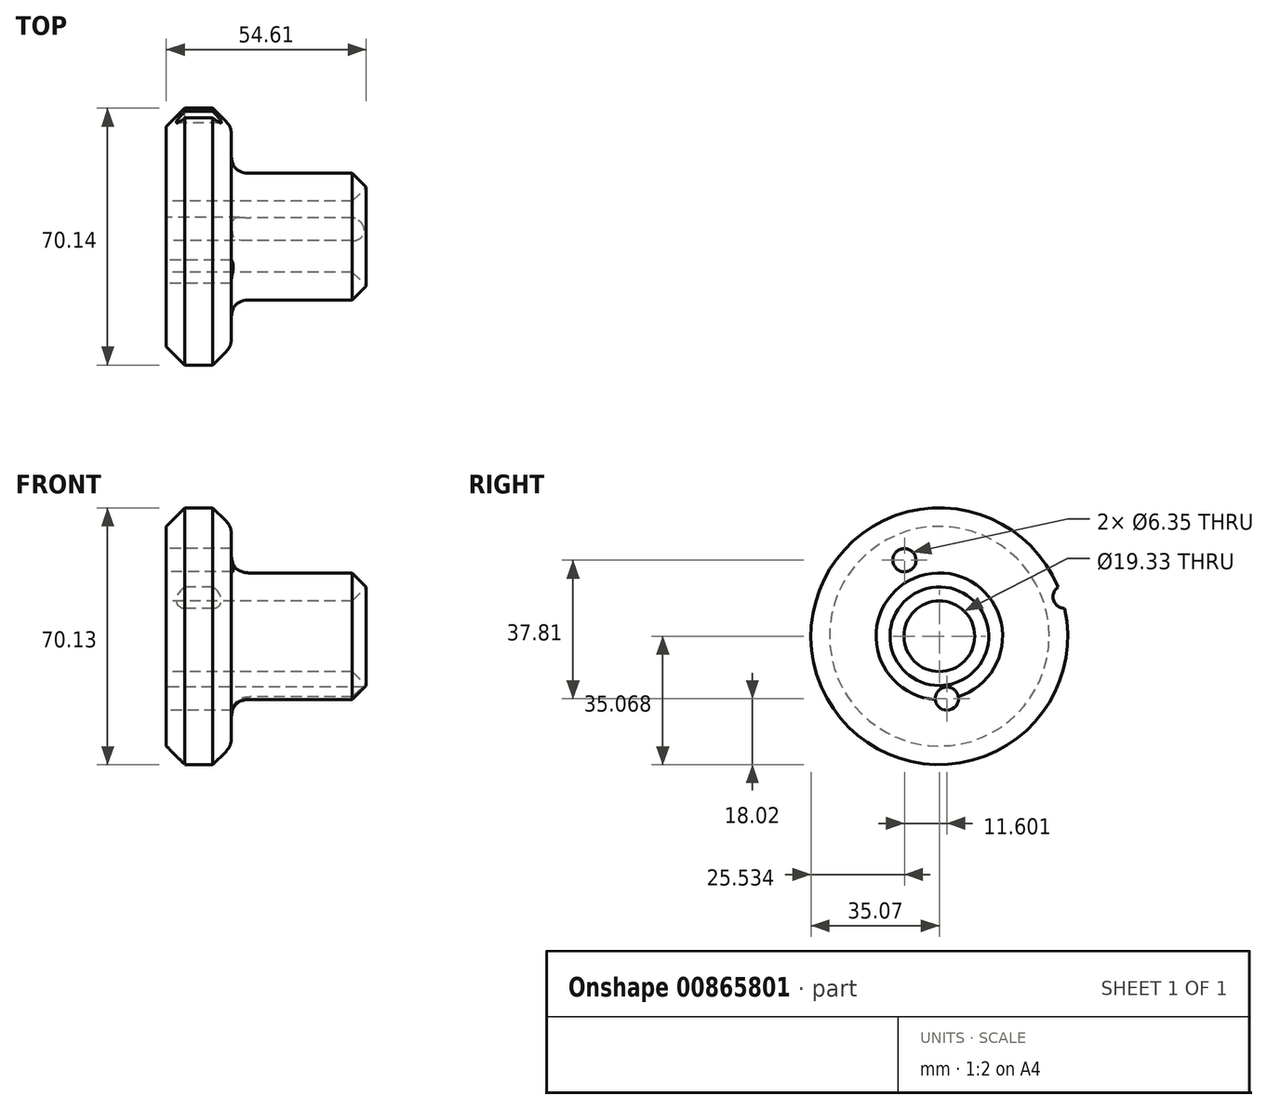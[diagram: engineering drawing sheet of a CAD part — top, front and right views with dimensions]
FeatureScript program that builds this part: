
annotation { "Feature Type Name" : "Feature", "Feature Type Description" : "" }
export const myFeature = defineFeature(function(context is Context, id is Id, definition is map)
    precondition{}
    {
        {
            var Q0;
            Q0=qCreatedBy(makeId("Front.planeOp"),FACE);
            var sketch = newSketch(context, id + "F0", { "sketchPlane" : qUnion([Q0])});
            skLineSegment(sketch, "E0", {"start": v(-39.33, 17.05) * mm, "end": v(50.95, 17.05) * mm, "construction": true});
            skLineSegment(sketch, "E1.bottom", {"start": v(-29.5, 52.11) * mm, "end": v(-11.71, 52.11) * mm});
            skLineSegment(sketch, "E1.top", {"start": v(-29.5, 26.71) * mm, "end": v(-11.71, 26.71) * mm});
            skLineSegment(sketch, "E1.left", {"start": v(-29.5, 52.11) * mm, "end": v(-29.5, 26.71) * mm});
            skLineSegment(sketch, "E1.right", {"start": v(-11.71, 52.11) * mm, "end": v(-11.71, 26.71) * mm});
            skLineSegment(sketch, "E2.bottom", {"start": v(-11.71, 34.33) * mm, "end": v(26.39, 34.33) * mm});
            skLineSegment(sketch, "E2.top", {"start": v(-11.71, 26.71) * mm, "end": v(26.39, 26.71) * mm});
            skLineSegment(sketch, "E2.left", {"start": v(-11.71, 34.33) * mm, "end": v(-11.71, 26.71) * mm});
            skLineSegment(sketch, "E2.right", {"start": v(26.39, 34.33) * mm, "end": v(26.39, 26.71) * mm});
            skSolve(sketch);
        }
        {
            var Q0;
            Q0 = qSketchRegion(id + "F0", true);
            var Q1;
            Q1=sQuery(id+"F0.wireOp",EDGE,"E0");
            revolve(context, id + "F1", {"surfaceOperationType" : NewSurfaceOperationType.NEW, "entities" : qUnion([Q0]), "axis" : qUnion([Q1]), "revolveType" : RevolveType.FULL});
        }
        {
            var Q0;
            Q0=makeQuery(id+"F1.opRevolve","SWEPT_EDGE",EDGE,{"disambiguationData":[OSD([sQuery(id+"F0.wireOp",EDGE,"E1.bottom"),sQuery(id+"F0.wireOp",EDGE,"E1.left")])]});
            var Q1;
            Q1=makeQuery(id+"F1.opRevolve","SWEPT_EDGE",EDGE,{"disambiguationData":[OSD([sQuery(id+"F0.wireOp",EDGE,"E1.bottom"),sQuery(id+"F0.wireOp",EDGE,"E1.right")])]});
            var Q2;
            Q2=makeQuery(id+"F1.opRevolve","SWEPT_EDGE",EDGE,{"disambiguationData":[OSD([sQuery(id+"F0.wireOp",EDGE,"E2.bottom"),sQuery(id+"F0.wireOp",EDGE,"E2.right")])]});
            chamfer(context, id + "F2", {"entities" : qUnion([Q0, Q1, Q2]), "width" : 5.08 * mm, "tangentPropagation" : true});
        }
        {
            var Q0;
            Q0=makeQuery(id+"F1.opRevolve","SWEPT_EDGE",EDGE,{"disambiguationData":[OSD([sQuery(id+"F0.wireOp",EDGE,"E1.right"),sQuery(id+"F0.wireOp",EDGE,"E2.bottom"),sQuery(id+"F0.wireOp",EDGE,"E2.left")])]});
            var Q1;
            {var subQ0=sQuery(id+"F0.wireOp",EDGE,"E1.right");Q1=makeQuery(id+"F2.opChamfer","BLEND_EDGE",EDGE,{"blendedFrom":[makeQuery(id+"F1.opRevolve","SWEPT_EDGE",EDGE,{"disambiguationData":[OSD([sQuery(id+"F0.wireOp",EDGE,"E1.bottom"),subQ0])]}),makeQuery(id+"F1.opRevolve","SWEPT_FACE",FACE,{"disambiguationData":[OSD([subQ0])]})],"blendedInto":[makeQuery(id+"F1.opRevolve","SWEPT_FACE",FACE,{"disambiguationData":[OSD([subQ0])]})]});}
            fillet(context, id + "F3", {"entities" : qUnion([Q0, Q1]), "radius" : 5.08 * mm, "tangentPropagation" : true, "rho" : 0.5, "crossSection" : FilletCrossSection.CONIC, "allowEdgeOverflow" : false});
        }
        {
            var Q0;
            Q0=makeQuery(id+"F1.opRevolve","SWEPT_EDGE",EDGE,{"disambiguationData":[OSD([sQuery(id+"F0.wireOp",EDGE,"E2.top"),sQuery(id+"F0.wireOp",EDGE,"E2.right")])]});
            chamfer(context, id + "F4", {"entities" : qUnion([Q0]), "width" : 5.08 * mm, "tangentPropagation" : true});
        }
        {
            var Q0;
            Q0=makeQuery(id+"F1.opRevolve","SWEPT_FACE",FACE,{"disambiguationData":[OSD([sQuery(id+"F0.wireOp",EDGE,"E1.left")])]});
            var sketch = newSketch(context, id + "F5", { "sketchPlane" : qUnion([Q0])});
            skCircle(sketch, "E3", {"center": v(-2.07, 0) * mm, "radius": 2.75 * mm});
            skSolve(sketch);
        }
        {
            var Q0;
            Q0=sQuery(id+"F5.wireOp",VERTEX,"E3.center");
            var Q1;
            Q1=makeQuery(id+"F1.opRevolve","SWEPT_BODY",BODY,{"disambiguationData":[OSD([sQuery(id+"F0.wireOp",EDGE,"E1.bottom"),sQuery(id+"F0.wireOp",EDGE,"E1.top"),sQuery(id+"F0.wireOp",EDGE,"E1.left"),sQuery(id+"F0.wireOp",EDGE,"E1.right"),sQuery(id+"F0.wireOp",EDGE,"E2.bottom"),sQuery(id+"F0.wireOp",EDGE,"E2.top"),sQuery(id+"F0.wireOp",EDGE,"E2.right")])]});
            hole(context, id + "F6", {"style" : HoleStyle.SIMPLE, "endStyle" : HoleEndStyle.THROUGH, "holeDiameter" : 6.35 * mm, "majorDiameter" : 6.35 * mm, "isTappedThrough" : true, "tappedDepth" : 12.7 * mm, "tapClearance" : 3, "locations" : qUnion([Q0]), "scope" : qUnion([Q1])});
        }
        {
            var Q0;
            Q0=makeQuery(id+"F1.opRevolve","SWEPT_FACE",FACE,{"disambiguationData":[OSD([sQuery(id+"F0.wireOp",EDGE,"E1.left")])]});
            var sketch = newSketch(context, id + "F7", { "sketchPlane" : qUnion([Q0])});
            skCircle(sketch, "E4", {"center": v(9.54, 37.8) * mm, "radius": 4.3 * mm});
            skSolve(sketch);
        }
        {
            var Q0;
            Q0=sQuery(id+"F7.wireOp",VERTEX,"E4.center");
            var Q1;
            Q1=makeQuery(id+"F1.opRevolve","SWEPT_BODY",BODY,{"disambiguationData":[OSD([sQuery(id+"F0.wireOp",EDGE,"E1.bottom"),sQuery(id+"F0.wireOp",EDGE,"E1.top"),sQuery(id+"F0.wireOp",EDGE,"E1.left"),sQuery(id+"F0.wireOp",EDGE,"E1.right"),sQuery(id+"F0.wireOp",EDGE,"E2.bottom"),sQuery(id+"F0.wireOp",EDGE,"E2.top"),sQuery(id+"F0.wireOp",EDGE,"E2.right")])]});
            hole(context, id + "F8", {"style" : HoleStyle.SIMPLE, "endStyle" : HoleEndStyle.THROUGH, "holeDiameter" : 6.35 * mm, "majorDiameter" : 6.35 * mm, "isTappedThrough" : true, "tappedDepth" : 12.7 * mm, "tapClearance" : 3, "locations" : qUnion([Q0]), "scope" : qUnion([Q1])});
        }
        {
            var Q0;
            Q0=makeQuery(id+"F1.opRevolve","SWEPT_FACE",FACE,{"disambiguationData":[OSD([sQuery(id+"F0.wireOp",EDGE,"E1.left")])]});
            var sketch = newSketch(context, id + "F9", { "sketchPlane" : qUnion([Q0])});
            skCircle(sketch, "E5", {"center": v(-34.23, 27.85) * mm, "radius": 3.23 * mm});
            skSolve(sketch);
        }
        {
            var Q0;
            Q0=sQuery(id+"F9.wireOp",VERTEX,"E5.center");
            var Q1;
            Q1=makeQuery(id+"F1.opRevolve","SWEPT_BODY",BODY,{"disambiguationData":[OSD([sQuery(id+"F0.wireOp",EDGE,"E1.bottom"),sQuery(id+"F0.wireOp",EDGE,"E1.top"),sQuery(id+"F0.wireOp",EDGE,"E1.left"),sQuery(id+"F0.wireOp",EDGE,"E1.right"),sQuery(id+"F0.wireOp",EDGE,"E2.bottom"),sQuery(id+"F0.wireOp",EDGE,"E2.top"),sQuery(id+"F0.wireOp",EDGE,"E2.right")])]});
            hole(context, id + "F10", {"style" : HoleStyle.SIMPLE, "endStyle" : HoleEndStyle.THROUGH, "holeDiameter" : 6.35 * mm, "majorDiameter" : 6.35 * mm, "isTappedThrough" : true, "tappedDepth" : 12.7 * mm, "tapClearance" : 3, "locations" : qUnion([Q0]), "scope" : qUnion([Q1])});
        }
    });
